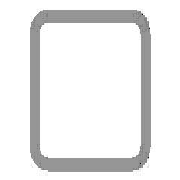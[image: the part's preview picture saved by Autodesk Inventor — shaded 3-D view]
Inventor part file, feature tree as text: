
AUTODESK INVENTOR PART (.ipt)
format: ipt  version: 2024 (Build 280153000, 153)  size: 129,024 bytes
history: native  units: mm (DEFAULTED — no unit token found)
features: other x4, extrude x1, sketch x1, plane x1
ambient origin geometry x8: Origin, YZ Plane, XZ Plane, XY Plane, X Axis, Y Axis, Z Axis, Center Point
bodies: Solid1 (feature_tree)
feature tree (7):
  parser-record x1  (decoder bookkeeping rows leaked as tree rows — omitted from the tree; the rows remain in map.json)
  other  "Driven Length"
  other  "Plano inicial"
  other  "Plano final"
  extrude  "Cuerpo"  TaperAngle=0.0deg  [1 undecoded]
  sketch  "Sketch3"  dims[d3=2090.0mm d4=0.0mm d10=50.8mm d11=50.8mm d12=3.175mm d13=-0.0mm d14=2090.0mm d15=25.4mm d16=25.4mm d17=6.35mm d18=90.0deg d19=2090.0mm]
  plane  "Work Plane3"
note: 1 required parameter value undecoded (feature->parameter linkage not recoverable at this tier; creation-order binding heuristic only, values carry confidence <= 0.55)
